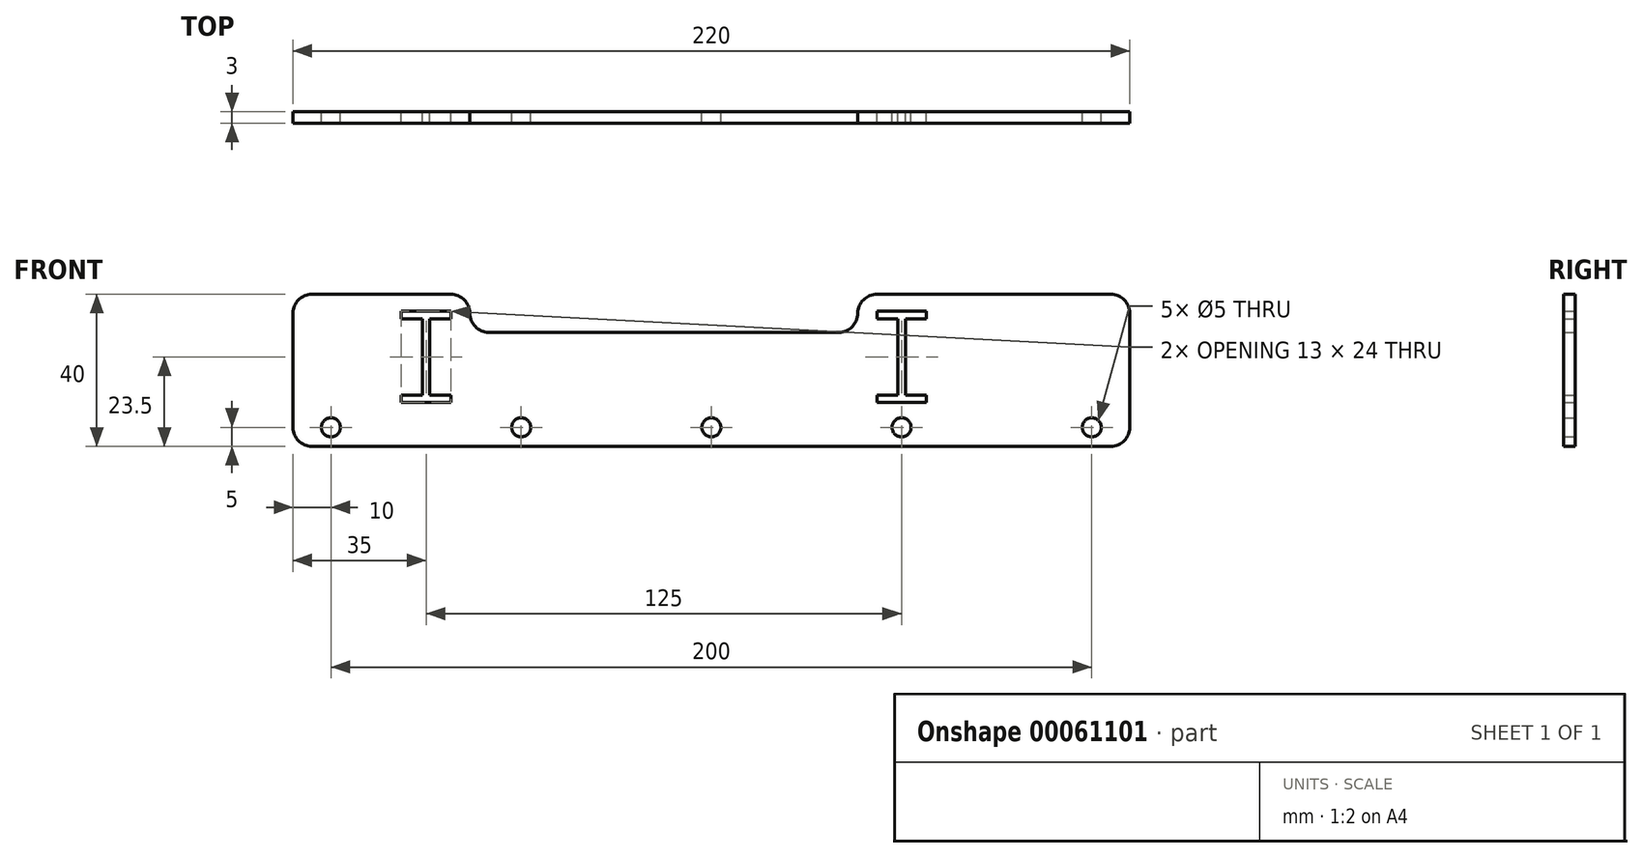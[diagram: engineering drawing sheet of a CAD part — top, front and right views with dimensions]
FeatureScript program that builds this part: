
annotation { "Feature Type Name" : "Feature", "Feature Type Description" : "" }
export const myFeature = defineFeature(function(context is Context, id is Id, definition is map)
    precondition{}
    {
        {
            var Q0;
            Q0=qCreatedBy(makeId("Front.planeOp"),FACE);
            var sketch = newSketch(context, id + "F0", { "sketchPlane" : qUnion([Q0])});
            skLineSegment(sketch, "E0.rect.bottom", {"start": v(-105, 20) * mm, "end": v(-68.5, 20) * mm});
            skLineSegment(sketch, "E0.rect.top", {"start": v(-105, -20) * mm, "end": v(105, -20) * mm});
            skLineSegment(sketch, "E0.rect.left", {"start": v(-110, 15) * mm, "end": v(-110, -15) * mm});
            skLineSegment(sketch, "E0.rect.right", {"start": v(110, 15) * mm, "end": v(110, -15) * mm});
            skPoint(sketch, "E0.rect.middle", {"position": v(0, 0) * mm});
            skCircle(sketch, "E1", {"center": v(-100, -15) * mm, "radius": 2.5 * mm});
            skCircle(sketch, "E2.1.0.0", {"center": v(-50, -15) * mm, "radius": 2.5 * mm});
            skCircle(sketch, "E2.2.0.0", {"center": v(0, -15) * mm, "radius": 2.5 * mm});
            skCircle(sketch, "E2.3.0.0", {"center": v(50, -15) * mm, "radius": 2.5 * mm});
            skCircle(sketch, "E2.4.0.0", {"center": v(100, -15) * mm, "radius": 2.5 * mm});
            skLineSegment(sketch, "E2.direction1", {"start": v(-100, -15) * mm, "end": v(-50, -15) * mm, "construction": true});
            skLineSegment(sketch, "E3", {"start": v(-81.5, 15.5) * mm, "end": v(-68.5, 15.5) * mm});
            skLineSegment(sketch, "E4", {"start": v(-68.5, 15.5) * mm, "end": v(-68.5, 13.5) * mm});
            skLineSegment(sketch, "E5", {"start": v(-68.5, 13.5) * mm, "end": v(-74, 13.5) * mm});
            skLineSegment(sketch, "E6", {"start": v(-74, 13.5) * mm, "end": v(-74, -6.5) * mm});
            skLineSegment(sketch, "E7", {"start": v(-74, -6.5) * mm, "end": v(-68.5, -6.5) * mm});
            skLineSegment(sketch, "E8", {"start": v(-68.5, -6.5) * mm, "end": v(-68.5, -8.5) * mm});
            skLineSegment(sketch, "E9", {"start": v(-68.5, -8.5) * mm, "end": v(-81.5, -8.5) * mm});
            skLineSegment(sketch, "E10", {"start": v(-81.5, -8.5) * mm, "end": v(-81.5, -6.5) * mm});
            skLineSegment(sketch, "E11", {"start": v(-81.5, -6.5) * mm, "end": v(-76, -6.5) * mm});
            skLineSegment(sketch, "E12", {"start": v(-76, -6.5) * mm, "end": v(-76, 13.5) * mm});
            skLineSegment(sketch, "E13", {"start": v(-76, 13.5) * mm, "end": v(-81.5, 13.5) * mm});
            skLineSegment(sketch, "E14", {"start": v(-81.5, 13.5) * mm, "end": v(-81.5, 15.5) * mm});
            skPoint(sketch, "E15", {"position": v(-75, -8.5) * mm});
            skPoint(sketch, "E16", {"position": v(-75, -15) * mm});
            skLineSegment(sketch, "E17.1.0.0", {"start": v(49, -6.5) * mm, "end": v(49, 13.5) * mm});
            skLineSegment(sketch, "E17.1.0.1", {"start": v(43.5, 15.5) * mm, "end": v(56.5, 15.5) * mm});
            skPoint(sketch, "E17.1.0.2", {"position": v(50, -8.5) * mm});
            skLineSegment(sketch, "E17.1.0.3", {"start": v(51, 13.5) * mm, "end": v(51, -6.5) * mm});
            skLineSegment(sketch, "E17.1.0.4", {"start": v(51, -6.5) * mm, "end": v(56.5, -6.5) * mm});
            skLineSegment(sketch, "E17.1.0.5", {"start": v(56.5, 13.5) * mm, "end": v(51, 13.5) * mm});
            skLineSegment(sketch, "E17.1.0.6", {"start": v(49, 13.5) * mm, "end": v(43.5, 13.5) * mm});
            skLineSegment(sketch, "E17.1.0.7", {"start": v(43.5, -6.5) * mm, "end": v(49, -6.5) * mm});
            skLineSegment(sketch, "E17.1.0.8", {"start": v(56.5, -8.5) * mm, "end": v(43.5, -8.5) * mm});
            skLineSegment(sketch, "E17.1.0.9", {"start": v(56.5, 15.5) * mm, "end": v(56.5, 13.5) * mm});
            skLineSegment(sketch, "E17.1.0.10", {"start": v(43.5, -8.5) * mm, "end": v(43.5, -6.5) * mm});
            skLineSegment(sketch, "E17.1.0.11", {"start": v(43.5, 13.5) * mm, "end": v(43.5, 15.5) * mm});
            skLineSegment(sketch, "E17.1.0.12", {"start": v(56.5, -6.5) * mm, "end": v(56.5, -8.5) * mm});
            skLineSegment(sketch, "E17.direction1", {"start": v(-76, -6.5) * mm, "end": v(49, -6.5) * mm, "construction": true});
            skLineSegment(sketch, "E18", {"start": v(-63.5, 15) * mm, "end": v(-63.5, 15) * mm});
            skLineSegment(sketch, "E19", {"start": v(-58.5, 10) * mm, "end": v(33.5, 10) * mm});
            skLineSegment(sketch, "E20", {"start": v(38.5, 15) * mm, "end": v(38.5, 15) * mm});
            skLineSegment(sketch, "E21.trimOffspring", {"start": v(43.5, 20) * mm, "end": v(105, 20) * mm});
            skPoint(sketch, "E22.visualSharp", {"position": v(-110, -20) * mm});
            skArc(sketch, "E22.filletArc", {"start": v(-110, -15) * mm, "mid": v(-108.54, -18.54) * mm, "end": v(-105, -20) * mm});
            skPoint(sketch, "E23.visualSharp", {"position": v(-110, 20) * mm});
            skArc(sketch, "E23.filletArc", {"start": v(-105, 20) * mm, "mid": v(-108.54, 18.54) * mm, "end": v(-110, 15) * mm});
            skPoint(sketch, "E24.visualSharp", {"position": v(-63.5, 20) * mm});
            skArc(sketch, "E24.filletArc", {"start": v(-63.5, 15) * mm, "mid": v(-64.96, 18.54) * mm, "end": v(-68.5, 20) * mm});
            skPoint(sketch, "E25.visualSharp", {"position": v(-63.5, 10) * mm});
            skArc(sketch, "E25.filletArc", {"start": v(-63.5, 15) * mm, "mid": v(-62.04, 11.46) * mm, "end": v(-58.5, 10) * mm});
            skPoint(sketch, "E26.visualSharp", {"position": v(38.5, 10) * mm});
            skArc(sketch, "E26.filletArc", {"start": v(33.5, 10) * mm, "mid": v(37.04, 11.46) * mm, "end": v(38.5, 15) * mm});
            skPoint(sketch, "E27.visualSharp", {"position": v(38.5, 20) * mm});
            skArc(sketch, "E27.filletArc", {"start": v(43.5, 20) * mm, "mid": v(39.96, 18.54) * mm, "end": v(38.5, 15) * mm});
            skPoint(sketch, "E28.visualSharp", {"position": v(110, 20) * mm});
            skArc(sketch, "E28.filletArc", {"start": v(110, 15) * mm, "mid": v(108.54, 18.54) * mm, "end": v(105, 20) * mm});
            skPoint(sketch, "E29.visualSharp", {"position": v(110, -20) * mm});
            skArc(sketch, "E29.filletArc", {"start": v(105, -20) * mm, "mid": v(108.54, -18.54) * mm, "end": v(110, -15) * mm});
            skSolve(sketch);
        }
        {
            var Q0;
            Q0=makeQuery(id+"F0.imprint","IMPRINT",FACE,{"disambiguationData":[TD([[makeQuery(id+"F0.imprint","IMPRINT",EDGE,{"derivedFrom":sQuery(id+"F0.wireOp",EDGE,"E0.rect.bottom")}),-1.0]])]});
            extrude(context, id + "F1", {"entities" : qUnion([Q0]), "depth" : 3 * mm});
        }
    });
